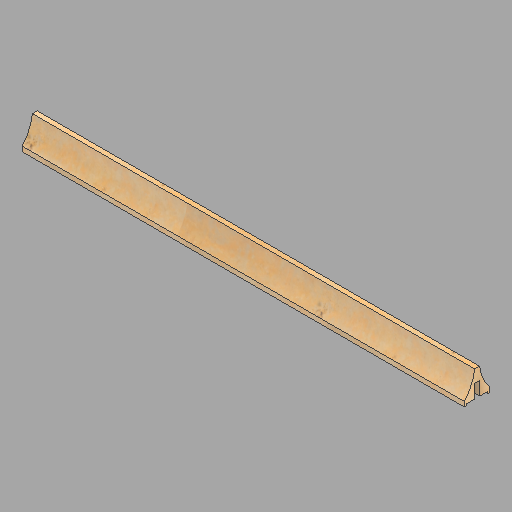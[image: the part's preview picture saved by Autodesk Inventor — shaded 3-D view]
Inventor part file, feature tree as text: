
AUTODESK INVENTOR PART (.ipt)
format: ipt  version: 2022.2 (Build 262287010, 287A)  size: 179,712 bytes
history: native  units: in
note: dims shown in document units (in); Inventor stores cm internally (conversion verified against a paired STEP export)
features: revolve x2, other x1, direct_edit x1
ambient origin geometry x8: Origin, YZ Plane, XZ Plane, XY Plane, X Axis, Y Axis, Z Axis, Center Point
bodies: Solid1 (feature_tree)
feature tree (4):
  other  "Lower Mull (2)"
  direct_edit  "Direct Edit1"
  revolve  "Rotate1"  [1 undecoded]
  revolve  "Rotate2"  Angle=180.0deg
note: 1 required parameter value undecoded (feature->parameter linkage not recoverable at this tier; creation-order binding heuristic only, values carry confidence <= 0.55)
